# Revit family: trixy_square_901723_002_e923
name_source: partatom
category: Lighting Fixtures
units: mm (PartAtom-declared; Revit-internal decimal feet)

## family parameters
Cut with Voids When Loaded = No
Host = Face
Light Source = No
Part Type = Normal
Room Calculation Point = No
Round Connector Dimension = Use Diameter
Shared = No

## types (1)
- MultiLumen 1 840 (1 x LED Modul 840, 1650 lm, 4000)
    Apparent Load = 14 VA
    Approval mark = CE
    CIE Flux Codes = 47 78 95 100 100
    Color Rendering = 80
    Color Temperature = 4000
    Default Elevation = 1800 mm
    Description = Series: TRIXY square
Ultra-flat square downlight suitable for recessed or surface installation. Housing made of UV-resistant polycarbonate. Perfect heat management with an aluminium heat sink. Diffuser made of plastic, transparent, with opal reflector foil. Lateral light emission (RZB SIDELITE technology) for homogeneous light distribution. MultiColour: With rear switching element, variable colour temperature 3000  K or 4000  K. Factory setting is 4000 K. MultiLumen: 3 steps adjustable luminous flux. Factory setting is the highest luminous flux. MultiCutOut: With adjustable spring clamps, different ceiling cut-outs can be individually adhered to. Suitable for ceiling cut-outs with Ø from > 120 to 260 mm. Suitable for recessed mounting in ceilings and surface mounting on ceilings and walls. Suitable for through-wiring. Driver integrated. 
Colour: white
Length: 300 mm
Width: 300 mm
Height: 25 mm
Cut-out diameter: 120-260 mm
Recess height: 82 mm
Luminaire: recess height: 25 mm
Lamp: LED
Socket: without socket
Colour temperature: 3000K, 4000K
Colour rendering index (CRI): 80
System power: 14 W
Rated luminous flux: 1650 lm
Luminous efficiency: 118 lm/W
System power 2: 22 W
Rated luminous flux 2: 2550 lm
Luminous efficiency 2: 116 lm/W
System power 3: 14 W
Rated luminous flux 3: 1550 lm
Luminous efficiency 3: 111 lm/W
System power 4: 22 W
Rated luminous flux 4: 2250 lm
Luminous efficiency 4: 102 lm/W
Control gear: Regulated power supply
Protection class: II
Type of protection: IP 20
    Height = 25 mm  [stored 0.082021 ft]
    Lamp = 1 x LED Modul 840
    Lamp Light Flux = 1650 lm
    Lamp count = 1
    Length = 300 mm
    Lifetime = 50000 h
    Luminous efficacy = 118 lm/W
    Manufacturer = RZB
    ModVariant = No
    Model = 901723.002
    Mounting Place = Ceiling
    Mounting Type = Surface mounted
    Number of Poles = 1
    OnlyDefault = Yes
    Power Factor = 1
    Product Name = TRIXY square
    Product group = Surface mounted downlights
    ProductGroupID = 302
    Protection Class = Protection class II
    Protection Degree = IP 20
    RLX_Detail_Level = 1
    RLX_Emergency_Light_Flux = 0 lm
    RLX_Emergency_Type = 0
    RLX_Emergency_Type_DB = No
    RlxData = <blob elided: 15681 chars, md5=19fa539b>
    Socket = socket
    Standby Power = 0 W
    System Light Flux = 1650 lm
    System Power = 14 W
    Type Comments = MultiLumen 1 840
    Type Image = 901723.002.jpg
    URL = http://relux.com
    VarID = multilumen_1_840
    Voltage = 230 V
    Voltage Range = 220-240 V
    Weight = 0.00 kg
    Width = 300 mm

note: [stored X ft] marks values corroborated as IEEE doubles in the binary element streams (Revit-internal decimal feet)

## geometry (parser evidence)
native form markers: Blend x4, Sweep x11
no freeform markers — native parametric forms only
